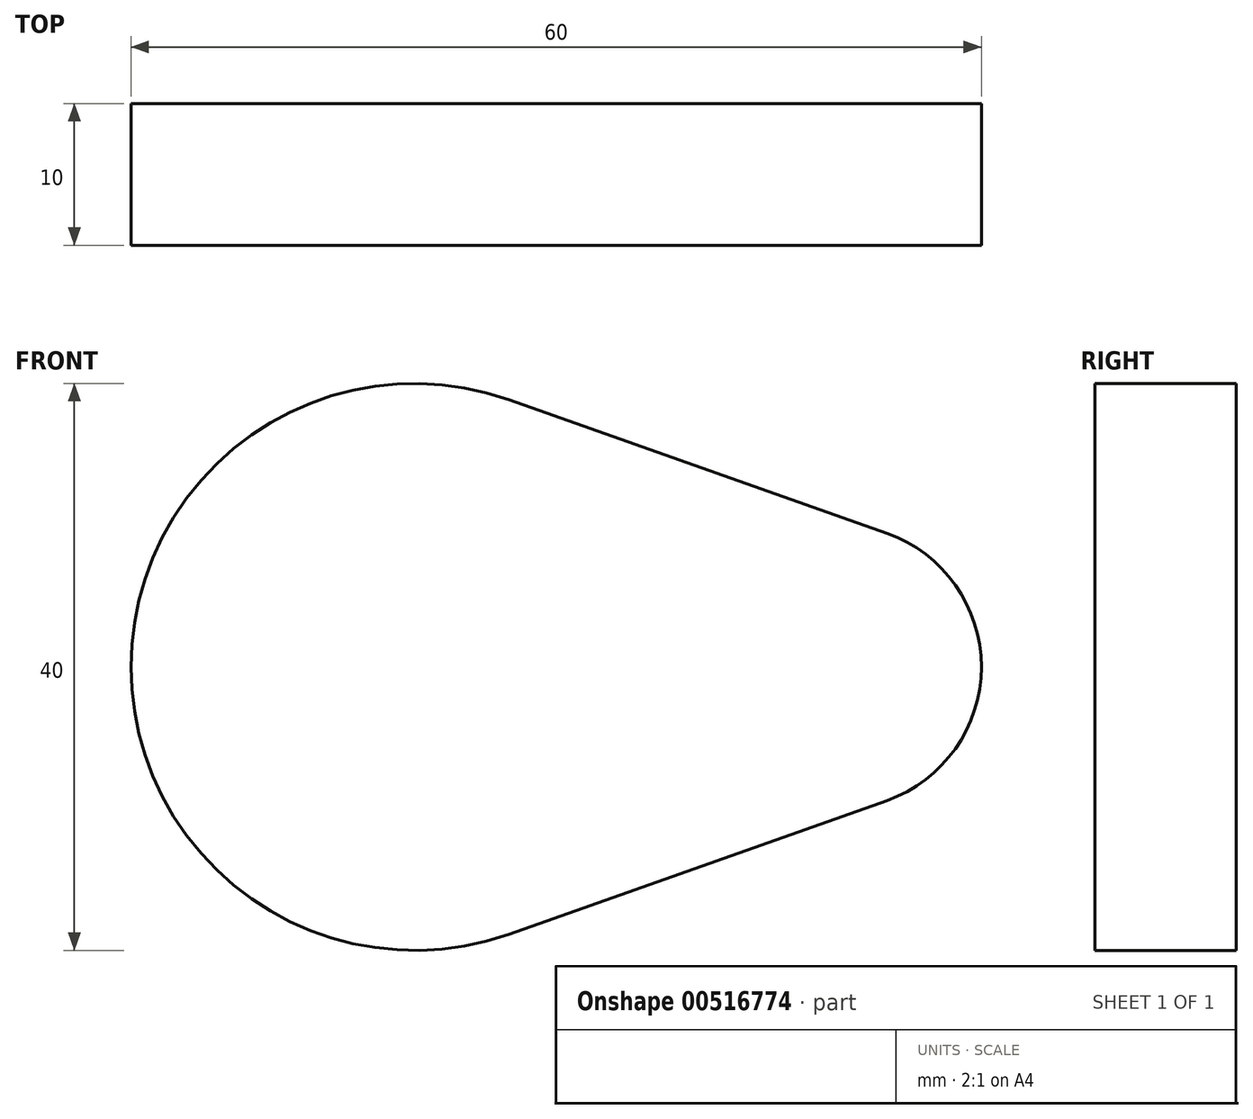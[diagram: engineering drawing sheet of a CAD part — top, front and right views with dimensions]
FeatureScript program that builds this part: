
annotation { "Feature Type Name" : "Feature", "Feature Type Description" : "" }
export const myFeature = defineFeature(function(context is Context, id is Id, definition is map)
    precondition{}
    {
        {
            var Q0;
            Q0=qCreatedBy(makeId("Front.planeOp"),FACE);
            var sketch = newSketch(context, id + "F0", { "sketchPlane" : qUnion([Q0])});
            skArc(sketch, "E0", {"start": v(6.67, 18.86) * mm, "mid": v(-20, 0) * mm, "end": v(6.67, -18.86) * mm});
            skArc(sketch, "E1", {"start": v(33.33, -9.43) * mm, "mid": v(40, 0) * mm, "end": v(33.33, 9.43) * mm});
            skLineSegment(sketch, "E2", {"start": v(6.67, 18.86) * mm, "end": v(33.33, 9.43) * mm});
            skLineSegment(sketch, "E3", {"start": v(6.67, -18.86) * mm, "end": v(33.33, -9.43) * mm});
            skSolve(sketch);
        }
        {
            var Q0;
            Q0 = qSketchRegion(id + "F0", true);
            extrude(context, id + "F1", {"entities" : qUnion([Q0]), "endBound" : BoundingType.SYMMETRIC, "depth" : 10 * mm, "offsetDistance" : 25.4 * mm, "hasDraft" : true, "draftAngle" : 0 * degree});
        }
    });
